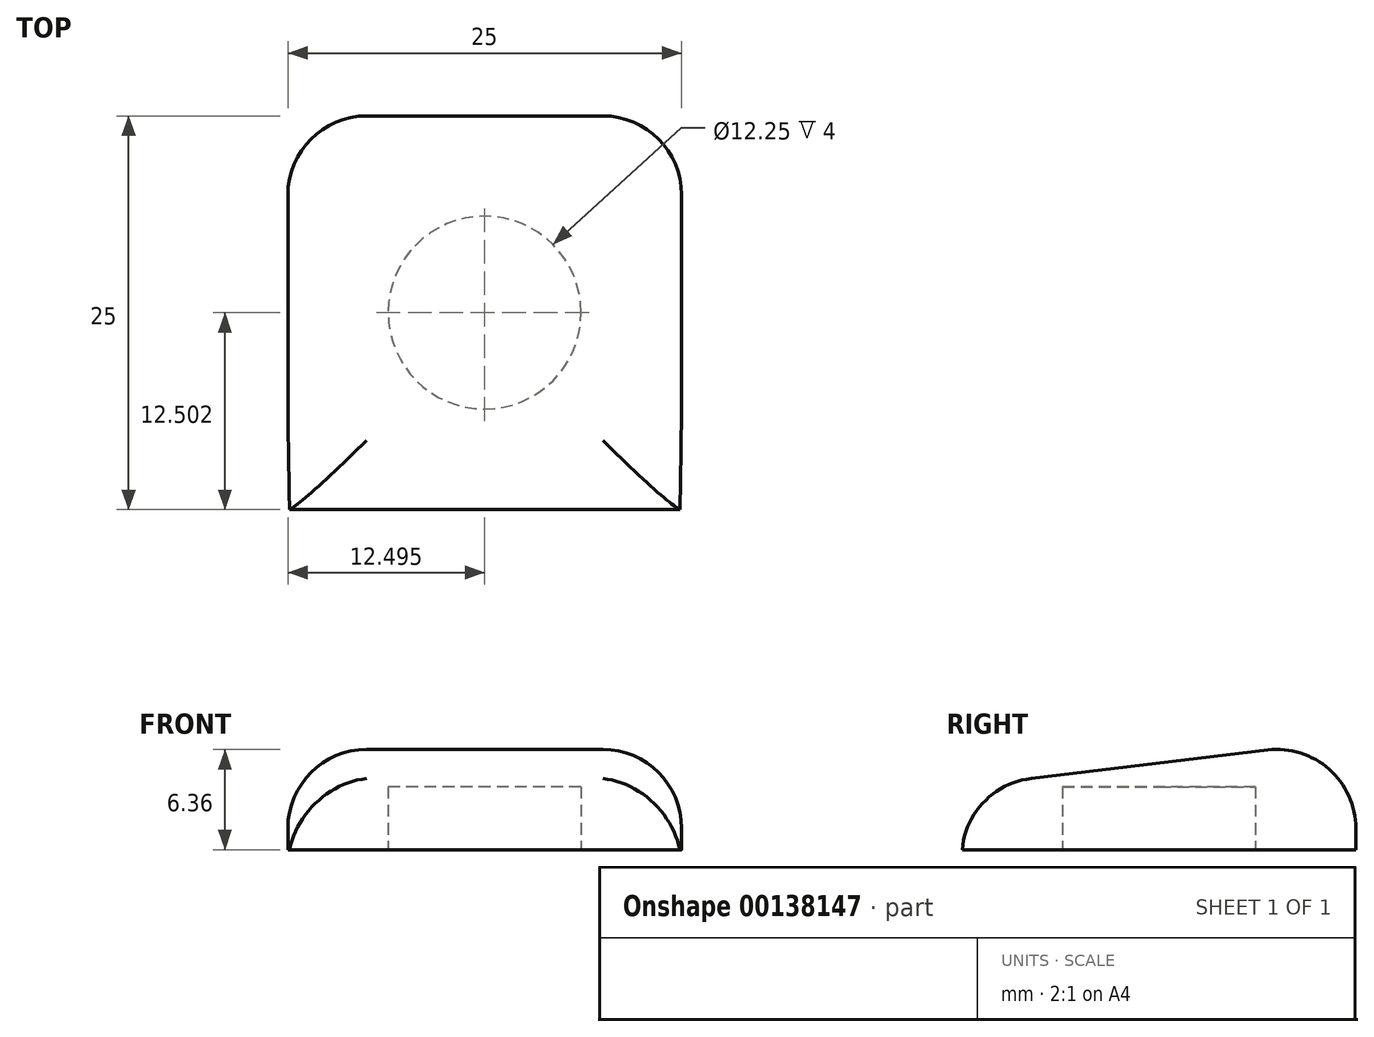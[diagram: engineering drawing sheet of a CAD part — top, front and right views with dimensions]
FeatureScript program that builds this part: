
annotation { "Feature Type Name" : "Feature", "Feature Type Description" : "" }
export const myFeature = defineFeature(function(context is Context, id is Id, definition is map)
    precondition{}
    {
        {
            var Q0;
            Q0=qCreatedBy(makeId("Right.planeOp"),FACE);
            var sketch = newSketch(context, id + "F0", { "sketchPlane" : qUnion([Q0])});
            skLineSegment(sketch, "E0", {"start": v(-9.1, 0) * mm, "end": v(15.9, 0) * mm});
            skLineSegment(sketch, "E1", {"start": v(15.9, 0) * mm, "end": v(15.9, 7) * mm});
            skLineSegment(sketch, "E2", {"start": v(-9.1, 0) * mm, "end": v(-9.1, 4) * mm});
            skLineSegment(sketch, "E3", {"start": v(-9.1, 4) * mm, "end": v(15.9, 7) * mm});
            skSolve(sketch);
        }
        {
            var Q0;
            Q0=makeQuery(id+"F0.imprint","IMPRINT",FACE,{"disambiguationData":[TD([[makeQuery(id+"F0.imprint","IMPRINT",EDGE,{"derivedFrom":sQuery(id+"F0.wireOp",EDGE,"E0")}),1.0]])]});
            extrude(context, id + "F1", {"entities" : qUnion([Q0]), "depth" : 25 * mm});
        }
        {
            var Q0;
            Q0=qCreatedBy(makeId("Top.planeOp"),FACE);
            var sketch = newSketch(context, id + "F2", { "sketchPlane" : qUnion([Q0])});
            skPoint(sketch, "E4", {"position": v(12.5, 0) * mm});
            skLineSegment(sketch, "E5", {"start": v(24.99, -9.12) * mm, "end": v(0, 15.94) * mm, "construction": true});
            skLineSegment(sketch, "E6", {"start": v(0, -9.08) * mm, "end": v(24.98, 15.92) * mm, "construction": true});
            skPoint(sketch, "E7", {"position": v(12.5, 3.41) * mm});
            skCircle(sketch, "E8", {"center": v(12.5, 3.41) * mm, "radius": 6.12 * mm});
            skSolve(sketch);
        }
        {
            var Q0;
            Q0=makeQuery(id+"F1.opExtrude","CAP_EDGE",EDGE,{"disambiguationData":[OSD([sQuery(id+"F0.wireOp",EDGE,"E3")])],"isStart":true});
            var Q1;
            Q1=makeQuery(id+"F1.opExtrude","SWEPT_EDGE",EDGE,{"disambiguationData":[OSD([sQuery(id+"F0.wireOp",EDGE,"E2"),sQuery(id+"F0.wireOp",EDGE,"E3")])]});
            var Q2;
            Q2=makeQuery(id+"F1.opExtrude","CAP_EDGE",EDGE,{"disambiguationData":[OSD([sQuery(id+"F0.wireOp",EDGE,"E3")])],"isStart":false});
            var Q3;
            Q3=makeQuery(id+"F1.opExtrude","SWEPT_EDGE",EDGE,{"disambiguationData":[OSD([sQuery(id+"F0.wireOp",EDGE,"E1"),sQuery(id+"F0.wireOp",EDGE,"E3")])]});
            var Q4;
            Q4=makeQuery(id+"F1.opExtrude","CAP_EDGE",EDGE,{"disambiguationData":[OSD([sQuery(id+"F0.wireOp",EDGE,"E1")])],"isStart":true});
            var Q5;
            Q5=makeQuery(id+"F1.opExtrude","CAP_EDGE",EDGE,{"disambiguationData":[OSD([sQuery(id+"F0.wireOp",EDGE,"E1")])],"isStart":false});
            fillet(context, id + "F3", {"entities" : qUnion([Q0, Q1, Q2, Q3, Q4, Q5]), "radius" : 5 * mm, "tangentPropagation" : true, "allowEdgeOverflow" : false});
        }
        {
            var Q0;
            Q0=makeQuery(id+"F2.imprint","IMPRINT",FACE,{"disambiguationData":[TD([[makeQuery(id+"F2.imprint","IMPRINT",EDGE,{"derivedFrom":sQuery(id+"F2.wireOp",EDGE,"E8")}),1.0]])]});
            extrude(context, id + "F4", {"entities" : qUnion([Q0]), "operationType" : NewBodyOperationType.REMOVE, "depth" : 4 * mm});
        }
    });
